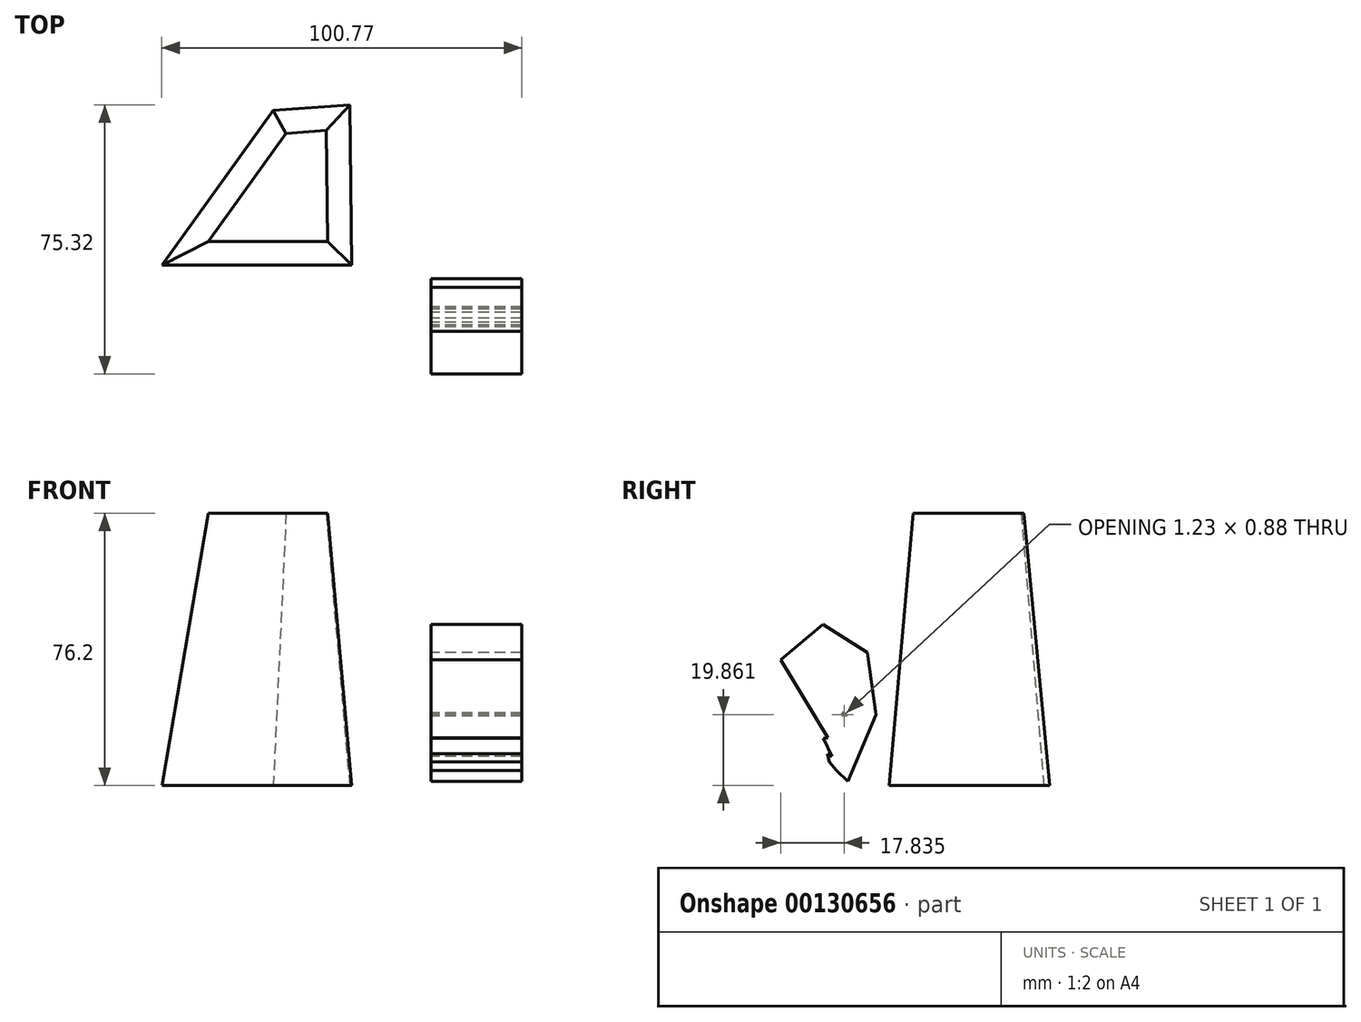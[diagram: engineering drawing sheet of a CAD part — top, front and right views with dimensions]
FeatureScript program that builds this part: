
annotation { "Feature Type Name" : "Feature", "Feature Type Description" : "" }
export const myFeature = defineFeature(function(context is Context, id is Id, definition is map)
    precondition{}
    {
        {
            var Q0;
            Q0=qCreatedBy(makeId("Top.planeOp"),FACE);
            var sketch = newSketch(context, id + "F0", { "sketchPlane" : qUnion([Q0])});
            skLineSegment(sketch, "E0", {"start": v(-98.42, -3.84) * mm, "end": v(74.48, 289.1) * mm});
            skLineSegment(sketch, "E1", {"start": v(-44.17, 16.56) * mm, "end": v(-75.37, -26.73) * mm});
            skLineSegment(sketch, "E2", {"start": v(-75.37, -26.73) * mm, "end": v(-22.26, -26.73) * mm});
            skLineSegment(sketch, "E3", {"start": v(-22.26, -26.73) * mm, "end": v(-22.78, 18.14) * mm});
            skLineSegment(sketch, "E4", {"start": v(-22.78, 18.14) * mm, "end": v(-44.17, 16.56) * mm});
            skSolve(sketch);
        }
        {
            var Q0;
            Q0=makeQuery(id+"F0.imprint","IMPRINT",FACE,{"disambiguationData":[TD([[makeQuery(id+"F0.imprint","IMPRINT",EDGE,{"derivedFrom":sQuery(id+"F0.wireOp",EDGE,"E1")}),1.0]])]});
            extrude(context, id + "F1", {"entities" : qUnion([Q0]), "depth" : 76.2 * mm, "hasDraft" : true, "draftAngle" : 5 * degree, "draftPullDirection" : true});
        }
        {
            var Q0;
            Q0=qCreatedBy(makeId("Right.planeOp"),FACE);
            var sketch = newSketch(context, id + "F2", { "sketchPlane" : qUnion([Q0])});
            skLineSegment(sketch, "E5", {"start": v(-35.86, 0) * mm, "end": v(-35.86, 0) * mm});
            skLineSegment(sketch, "E6", {"start": v(-35.86, 0) * mm, "end": v(-57.18, 35.2) * mm});
            skLineSegment(sketch, "E7", {"start": v(-57.18, 35.2) * mm, "end": v(-45.3, 45.03) * mm});
            skLineSegment(sketch, "E8", {"start": v(-45.3, 45.03) * mm, "end": v(-32.92, 37.27) * mm});
            skLineSegment(sketch, "E9", {"start": v(-32.92, 37.27) * mm, "end": v(-30.47, 19.8) * mm});
            skLineSegment(sketch, "E10", {"start": v(-30.47, 19.8) * mm, "end": v(-39.5, -1.45) * mm});
            skLineSegment(sketch, "E11", {"start": v(-39.5, -1.45) * mm, "end": v(-38.4, 1.17) * mm});
            skLineSegment(sketch, "E12", {"start": v(-38.4, 1.17) * mm, "end": v(-41.55, 4.14) * mm});
            skLineSegment(sketch, "E13", {"start": v(-41.55, 4.14) * mm, "end": v(-43.53, 6.58) * mm});
            skLineSegment(sketch, "E14", {"start": v(-43.53, 6.58) * mm, "end": v(-44.03, 8.85) * mm});
            skLineSegment(sketch, "E15", {"start": v(-44.03, 8.85) * mm, "end": v(-42.77, 8.1) * mm});
            skLineSegment(sketch, "E16", {"start": v(-42.77, 8.1) * mm, "end": v(-45.18, 13.2) * mm});
            skLineSegment(sketch, "E17", {"start": v(-45.18, 13.2) * mm, "end": v(-41.2, 13.6) * mm});
            skLineSegment(sketch, "E18", {"start": v(-41.2, 13.6) * mm, "end": v(-38.73, 20.12) * mm});
            skLineSegment(sketch, "E19", {"start": v(-38.73, 20.12) * mm, "end": v(-39.96, 20.3) * mm});
            skLineSegment(sketch, "E20", {"start": v(-39.96, 20.3) * mm, "end": v(-37.32, 17.88) * mm});
            skLineSegment(sketch, "E21", {"start": v(-37.32, 17.88) * mm, "end": v(-38.01, 13.91) * mm});
            skLineSegment(sketch, "E22", {"start": v(-38.01, 13.91) * mm, "end": v(-35.64, 11.3) * mm});
            skLineSegment(sketch, "E23", {"start": v(-35.64, 11.3) * mm, "end": v(-36.46, 5.7) * mm});
            skLineSegment(sketch, "E24", {"start": v(-36.46, 5.7) * mm, "end": v(-39.25, 9.12) * mm});
            skLineSegment(sketch, "E25", {"start": v(-39.25, 9.12) * mm, "end": v(-43.98, 18.99) * mm});
            skSolve(sketch);
        }
        {
            var Q0;
            Q0 = qSketchRegion(id + "F2", true);
            extrude(context, id + "F3", {"entities" : qUnion([Q0]), "depth" : 25.4 * mm});
        }
    });
